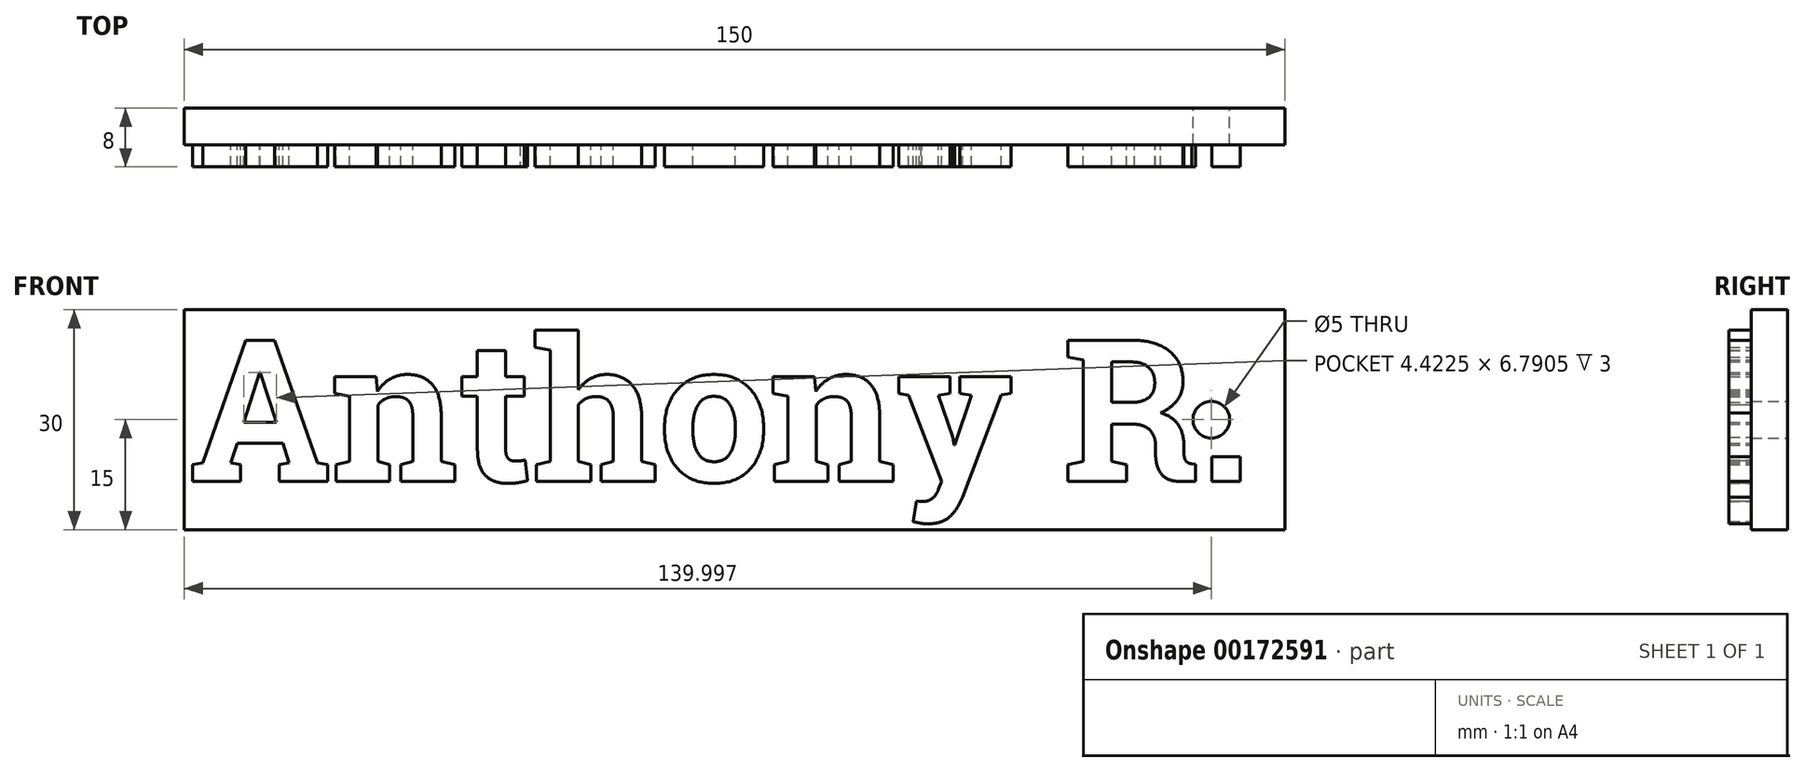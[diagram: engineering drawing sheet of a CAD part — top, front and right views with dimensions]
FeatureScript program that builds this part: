
annotation { "Feature Type Name" : "Feature", "Feature Type Description" : "" }
export const myFeature = defineFeature(function(context is Context, id is Id, definition is map)
    precondition{}
    {
        {
            var Q0;
            Q0=qCreatedBy(makeId("Front.planeOp"),FACE);
            var sketch = newSketch(context, id + "F0", { "sketchPlane" : qUnion([Q0])});
            skLineSegment(sketch, "E0.bottom", {"start": v(-74.73, 0) * mm, "end": v(75.27, 0) * mm});
            skLineSegment(sketch, "E0.top", {"start": v(-74.73, -30) * mm, "end": v(75.27, -30) * mm});
            skLineSegment(sketch, "E0.left", {"start": v(-74.73, 0) * mm, "end": v(-74.73, -30) * mm});
            skLineSegment(sketch, "E0.right", {"start": v(75.27, 0) * mm, "end": v(75.27, -30) * mm});
            skCircle(sketch, "E1", {"center": v(65.27, -15) * mm, "radius": 2.5 * mm});
            skSolve(sketch);
        }
        {
            var Q0;
            {var subQ1=sQuery(id+"F0.wireOp",EDGE,"E0.bottom");Q0=makeQuery(id+"F0.imprint","IMPRINT",FACE,{"disambiguationData":[TD([[makeQuery(id+"F0.imprint","IMPRINT",EDGE,{"derivedFrom":subQ1}),-1.0]])]});}
            extrude(context, id + "F1", {"entities" : qUnion([Q0]), "depth" : 5 * mm});
        }
        {
            var Q0;
            Q0=makeQuery(id+"F1.opExtrude","CAP_FACE",FACE,{"disambiguationData":[OSD([sQuery(id+"F0.wireOp",EDGE,"E0.bottom"),sQuery(id+"F0.wireOp",EDGE,"E0.top"),sQuery(id+"F0.wireOp",EDGE,"E0.left"),sQuery(id+"F0.wireOp",EDGE,"E0.right"),sQuery(id+"F0.wireOp",EDGE,"E1")])],"isStart":false});
            var sketch = newSketch(context, id + "F2", { "sketchPlane" : qUnion([Q0])});
            skText(sketch, "E2", { "text": "Anthony R.", "fontName": "RobotoSlab-Bold.ttf"});
            const initialGuessF2  = {"E2": [-0.07415, -0.02342, 1, 0, 0.01952]};
            skSetInitialGuess(sketch, initialGuessF2);
            skSolve(sketch);
        }
        {
            var Q0;
            Q0 = qSketchRegion(id + "F2", true);
            extrude(context, id + "F3", {"entities" : qUnion([Q0]), "operationType" : NewBodyOperationType.ADD, "depth" : 3 * mm});
        }
    });
